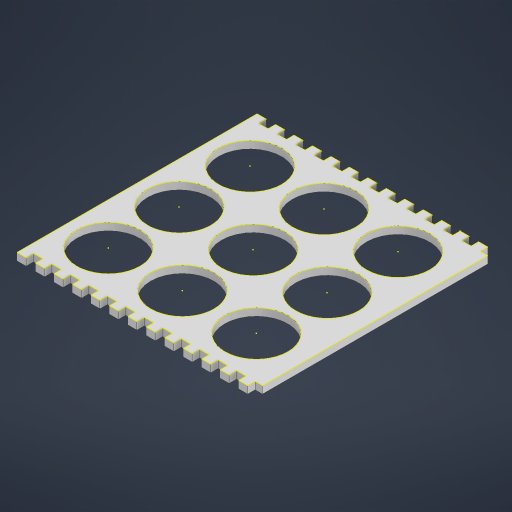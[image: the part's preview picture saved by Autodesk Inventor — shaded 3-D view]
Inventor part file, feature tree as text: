
AUTODESK INVENTOR PART (.ipt)
format: ipt  version: 2023 (Build 270158030, 158C)  size: 445,952 bytes
history: native  units: mm
features: sketch x3, extrude x2, mirror x1, projected_geometry x1
ambient origin geometry x8: Origin, YZ Plane, XZ Plane, XY Plane, X Axis, Y Axis, Z Axis, Center Point
bodies: Solid1 (feature_tree)
feature tree (7):
  extrude  "Extrusion1"  Depth=4.0mm TaperAngle=0.0deg
  mirror  "Mirror1"
  extrude  "Extrusion2"  Depth=6.5mm TaperAngle=0.0deg
  sketch  "Sketch3"
  sketch  "Sketch1"  dims[d0=180.0deg d1=4.0mm d2=0.0mm]
  sketch  "Sketch2"  dims[d3=132.004478mm d5=0.0mm d6=3.880396mm d7=47.003386mm d11=8.0mm d12=6.5mm d13=0.0mm]
  projected_geometry  "Projected Loop1"
